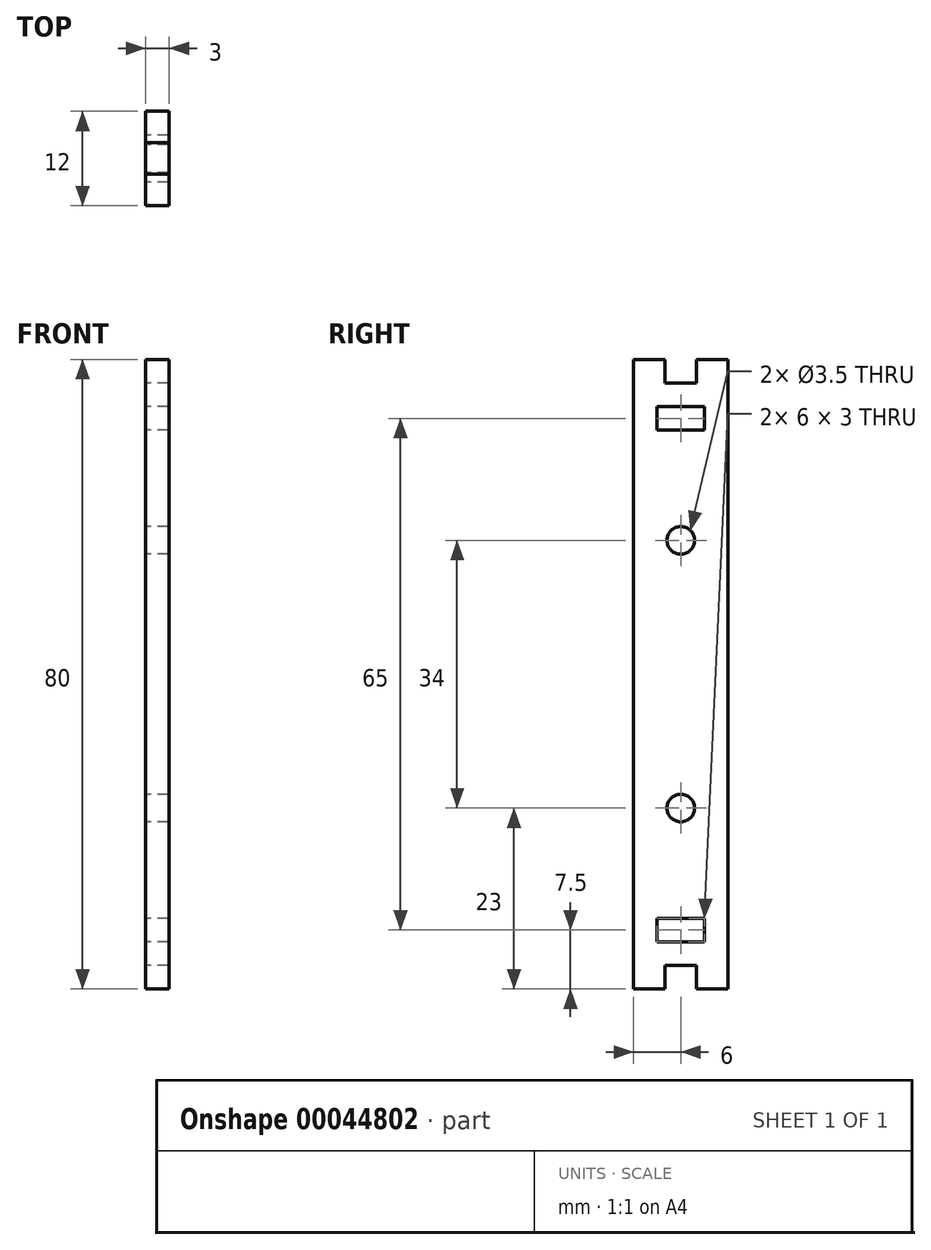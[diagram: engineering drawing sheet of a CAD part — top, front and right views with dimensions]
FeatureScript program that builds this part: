
annotation { "Feature Type Name" : "Feature", "Feature Type Description" : "" }
export const myFeature = defineFeature(function(context is Context, id is Id, definition is map)
    precondition{}
    {
        {
            var Q0;
            Q0=qCreatedBy(makeId("Right.planeOp"),FACE);
            var sketch = newSketch(context, id + "F0", { "sketchPlane" : qUnion([Q0])});
            skLineSegment(sketch, "E0.rect.bottom", {"start": v(6, 37) * mm, "end": v(-6, 37) * mm});
            skLineSegment(sketch, "E0.rect.top", {"start": v(6, -37) * mm, "end": v(-6, -37) * mm});
            skLineSegment(sketch, "E0.rect.left", {"start": v(6, 37) * mm, "end": v(6, -37) * mm});
            skLineSegment(sketch, "E0.rect.right", {"start": v(-6, 37) * mm, "end": v(-6, -37) * mm});
            skPoint(sketch, "E0.rect.middle", {"position": v(0, 0) * mm});
            skLineSegment(sketch, "E1.bottom", {"start": v(-3, -31) * mm, "end": v(3, -31) * mm});
            skLineSegment(sketch, "E1.top", {"start": v(-3, -34) * mm, "end": v(3, -34) * mm});
            skLineSegment(sketch, "E1.left", {"start": v(-3, -31) * mm, "end": v(-3, -34) * mm});
            skLineSegment(sketch, "E1.right", {"start": v(3, -31) * mm, "end": v(3, -34) * mm});
            skLineSegment(sketch, "E2.bottom", {"start": v(-3, 34) * mm, "end": v(3, 34) * mm});
            skLineSegment(sketch, "E2.top", {"start": v(-3, 31) * mm, "end": v(3, 31) * mm});
            skLineSegment(sketch, "E2.left", {"start": v(-3, 34) * mm, "end": v(-3, 31) * mm});
            skLineSegment(sketch, "E2.right", {"start": v(3, 34) * mm, "end": v(3, 31) * mm});
            skCircle(sketch, "E3", {"center": v(0, 17) * mm, "radius": 1.75 * mm});
            skPoint(sketch, "E3.centerSnap0", {"position": v(0, 31) * mm});
            skPoint(sketch, "E4.centerSnap0", {"position": v(0, -31) * mm});
            skLineSegment(sketch, "E5.bottom", {"start": v(-6, 37) * mm, "end": v(-2, 37) * mm});
            skLineSegment(sketch, "E5.top", {"start": v(-6, 40) * mm, "end": v(-2, 40) * mm});
            skLineSegment(sketch, "E5.left", {"start": v(-6, 37) * mm, "end": v(-6, 40) * mm});
            skLineSegment(sketch, "E5.right", {"start": v(-2, 37) * mm, "end": v(-2, 40) * mm});
            skLineSegment(sketch, "E6.bottom", {"start": v(6, 37) * mm, "end": v(2, 37) * mm});
            skLineSegment(sketch, "E6.top", {"start": v(6, 40) * mm, "end": v(2, 40) * mm});
            skLineSegment(sketch, "E6.left", {"start": v(6, 37) * mm, "end": v(6, 40) * mm});
            skLineSegment(sketch, "E6.right", {"start": v(2, 37) * mm, "end": v(2, 40) * mm});
            skLineSegment(sketch, "E7", {"start": v(0, 37) * mm, "end": v(0, -37) * mm, "construction": true});
            skCircle(sketch, "E8", {"center": v(0, -17) * mm, "radius": 1.75 * mm});
            skLineSegment(sketch, "E9.bottom", {"start": v(-6, -37) * mm, "end": v(-2, -37) * mm});
            skLineSegment(sketch, "E9.top", {"start": v(-6, -40) * mm, "end": v(-2, -40) * mm});
            skLineSegment(sketch, "E9.left", {"start": v(-6, -37) * mm, "end": v(-6, -40) * mm});
            skLineSegment(sketch, "E9.right", {"start": v(-2, -37) * mm, "end": v(-2, -40) * mm});
            skLineSegment(sketch, "E10.bottom", {"start": v(6, -37) * mm, "end": v(2, -37) * mm});
            skLineSegment(sketch, "E10.top", {"start": v(6, -40) * mm, "end": v(2, -40) * mm});
            skLineSegment(sketch, "E10.left", {"start": v(6, -37) * mm, "end": v(6, -40) * mm});
            skLineSegment(sketch, "E10.right", {"start": v(2, -37) * mm, "end": v(2, -40) * mm});
            skSolve(sketch);
        }
        {
            var Q0;
            Q0=qSketchRegion(id+"F0",true);
            extrude(context, id + "F1", {"entities" : qUnion([Q0]), "depth" : 3 * mm});
        }
    });
